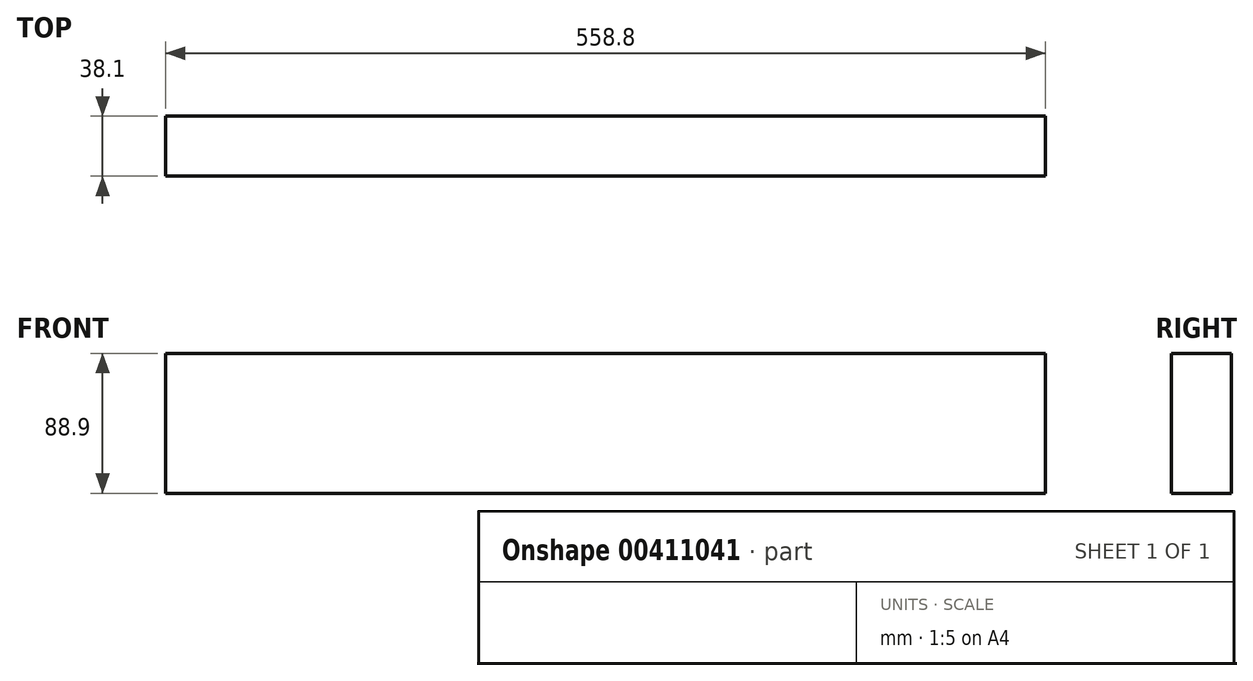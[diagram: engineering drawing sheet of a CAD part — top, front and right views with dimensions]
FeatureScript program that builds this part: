
annotation { "Feature Type Name" : "Feature", "Feature Type Description" : "" }
export const myFeature = defineFeature(function(context is Context, id is Id, definition is map)
    precondition{}
    {
        {
            var Q0;
            Q0=qCreatedBy(makeId("Right.planeOp"),FACE);
            var sketch = newSketch(context, id + "F0", { "sketchPlane" : qUnion([Q0])});
            skLineSegment(sketch, "E0.bottom", {"start": v(19.05, -44.45) * mm, "end": v(-19.05, -44.45) * mm});
            skLineSegment(sketch, "E0.top", {"start": v(19.05, 44.45) * mm, "end": v(-19.05, 44.45) * mm});
            skLineSegment(sketch, "E0.left", {"start": v(19.05, -44.45) * mm, "end": v(19.05, 44.45) * mm});
            skLineSegment(sketch, "E0.right", {"start": v(-19.05, -44.45) * mm, "end": v(-19.05, 44.45) * mm});
            skPoint(sketch, "E0.middle", {"position": v(0, 0) * mm});
            skSolve(sketch);
        }
        {
            var Q0;
            Q0=makeQuery(id+"F0.imprint","IMPRINT",FACE,{"disambiguationData":[TD([[makeQuery(id+"F0.imprint","IMPRINT",EDGE,{"derivedFrom":sQuery(id+"F0.wireOp",EDGE,"E0.bottom")}),-1.0]])]});
            extrude(context, id + "F1", {"entities" : qUnion([Q0]), "depth" : 558.8 * mm});
        }
    });
